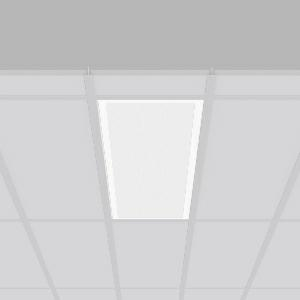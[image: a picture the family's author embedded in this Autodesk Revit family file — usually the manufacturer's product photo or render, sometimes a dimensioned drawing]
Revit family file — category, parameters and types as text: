
# Revit family: sidelite_eco_672374_002_04_33f8
name_source: partatom
category: Lighting Fixtures
units: mm (PartAtom-declared; Revit-internal decimal feet)

## family parameters
Cut with Voids When Loaded = No
Host = Face
Light Source = No
Part Type = Normal
Room Calculation Point = No
Round Connector Dimension = Use Diameter
Shared = No

## types (1)
- SIDELITE ECO (1 x LED Modul 830, 3150 lm, 3000)
    Apparent Load = 29 VA
    CIE Flux Codes = 60 87 97 100 100
    Color Rendering = 80
    Color Temperature = 3000
    Default Elevation = 1800 mm
    Description = Series: SIDELITE ECO
Highly economical recessed luminaire with progressive LED technology. For escape route illumination. Frame made of aluminium, powder-coated. Diffuser plastic microprismatic. Lightguide and diffuser made of non-yellowing plastic (PMMA). Lateral light emission (RZB SIDELITE technology) for homogeneous light distribution. External driver. Self-contained system with automatic self-test and feedback to the RZB monitoring system MULTIDIGIT. External driver with simple plug-in locking system. Extended connection cable (1.90 m). 
Colour: white
Length: 1245 mm
Width: 308 mm
Cut-out length: 1220 mm
Cut-out width: 285 mm
Recess height: 160 mm
Luminaire: recess height: 40 mm
Weight: 4.7 kg
Operating mode: maintained power mode
Duration time: 3 h
Lamp: LED
Socket: without socket
Colour temperature: 3000K
Colour rendering index (CRI): 80
System power: 29 W
Rated luminous flux: 3150 lm
Luminous flux, emergency: 460 lm
System power, emergency: -
Control gear: Regulated power supply
Protection class: I
Type of protection: IP 40
    Height = 0 mm  [stored 0 ft]
    Lamp = 1 x LED Modul 830
    Lamp Light Flux = 3150 lm
    Lamp count = 1
    Length = 1245 mm
    Lifetime = 50000 h
    Luminous efficacy = 109 lm/W
    Manufacturer = RZB
    ModVariant = No
    Model = 672374.002.04
    Mounting Place = Ceiling
    Mounting Type = Recessed
    Number of Poles = 1
    OnlyDefault = Yes
    Power Factor = 1
    Product Name = SIDELITE ECO
    Product group = Recessed modular luminaires
    ProductGroupID = 406
    Protection Class = Protection class I
    Protection Degree = IP 40
    RLX_Detail_Level = 1
    RLX_Emergency_Light_Flux = 460 lm
    RLX_Emergency_Type = 3
    RLX_Emergency_Type_DB = Yes
    RlxData = <blob elided: 34229 chars, md5=e11968e3>
    Socket = socket
    Standby Power = 0 W
    System Light Flux = 3150 lm
    System Power = 29 W
    Type Comments = Product without accessories
    Type Image = 312368.002.jpg
    URL = http://relux.com
    VarID = ---
    Voltage = 230 V
    Voltage Range = 220-240 V
    Weight = 0.00 kg
    Width = 308 mm

note: [stored X ft] marks values corroborated as IEEE doubles in the binary element streams (Revit-internal decimal feet)

## geometry (parser evidence)
native form markers: Blend x4, Sweep x10
no freeform markers — native parametric forms only
